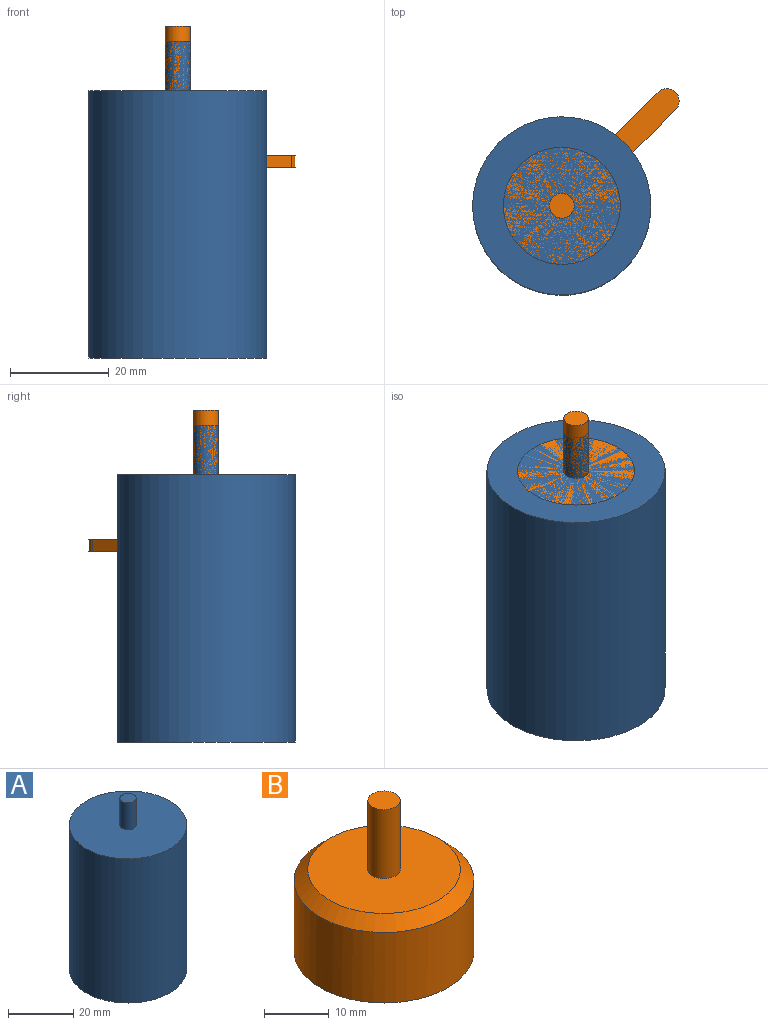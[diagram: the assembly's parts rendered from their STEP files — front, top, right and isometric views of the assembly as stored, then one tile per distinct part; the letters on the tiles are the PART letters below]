
ASSEMBLY  parts=2 mates=1
PART A: 5 faces, bbox 36x36x64 mm
  f0: cylinder r=18mm len=54mm, axis (0,0,1), area 6107.3mm2, adj f1,f4
  f1: plane 36x36mm, normal (0,0,1), area 998.2mm2, adj f0,f2
  f2: cylinder r=2.5mm len=10mm, axis (0,0,1), area 157.1mm2, adj f1,f3
  f3: plane 5x5mm, normal (0,0,1), area 19.6mm2, adj f2
  f4: plane 36x36mm, normal (0,0,-1), area 1017.9mm2, adj f0
PART B: 18 faces, bbox 37.7x37.7x28.6 mm
  f0: plane 37.66x37.66mm, normal (0,0,-1), area 673.5mm2, adj f1,f3,f4,f5,f7,f9,f11,f13
  f1: cylinder r=13.95mm len=27.9mm, axis (0,0,-1), area 1160.1mm2, adj f0,f2,f3,f4,f16
  f2: plane 15.78x15.78mm, normal (0,0,1), area 90.4mm2, adj f1,f3,f4,f5
  f3: plane 11.51x11.51mm, normal (0.71,-0.71,0), area 40.7mm2, adj f0,f1,f2,f5
  f4: plane 11.51x11.51mm, normal (-0.71,0.71,0), area 40.7mm2, adj f0,f1,f2,f5
  f5: cylinder r=2.5mm len=4.27mm, axis (0,0,1), area 19.6mm2, adj f0,f2,f3,f4
  f6: plane 3x3mm, normal (0,0,-1), area 7.1mm2, adj f7
  f7: cylinder r=1.5mm len=10mm, axis (0,0,1), area 94.2mm2, adj f0,f6
  f8: plane 3x3mm, normal (0,0,-1), area 7.1mm2, adj f9
  f9: cylinder r=1.5mm len=10mm, axis (0,0,1), area 94.2mm2, adj f0,f8
  f10: plane 3x3mm, normal (0,0,-1), area 7.1mm2, adj f11
  f11: cylinder r=1.5mm len=10mm, axis (0,0,1), area 94.2mm2, adj f0,f10
  f12: plane 3x3mm, normal (0,0,-1), area 7.1mm2, adj f13
  f13: cylinder r=1.5mm len=10mm, axis (0,0,1), area 94.2mm2, adj f0,f12
  f14: cylinder r=2.5mm len=13.1mm, axis (0,0,-1), area 205.8mm2, adj f15,f17
  f15: plane 23.66x23.66mm, normal (0,0,1), area 419.9mm2, adj f14,f16
  f16: cone r=13.95mm half-angle=45deg, axis (0,0,-1), area 243mm2, adj f1,f15
  f17: plane 5x5mm, normal (0,0,1), area 19.6mm2, adj f14
PLACE A at identity
PLACE B t=(0,0,11.5)mm
MATE fastened B.f1 <-> A.f0  axis (0,0,1) through (0,0,27)mm
